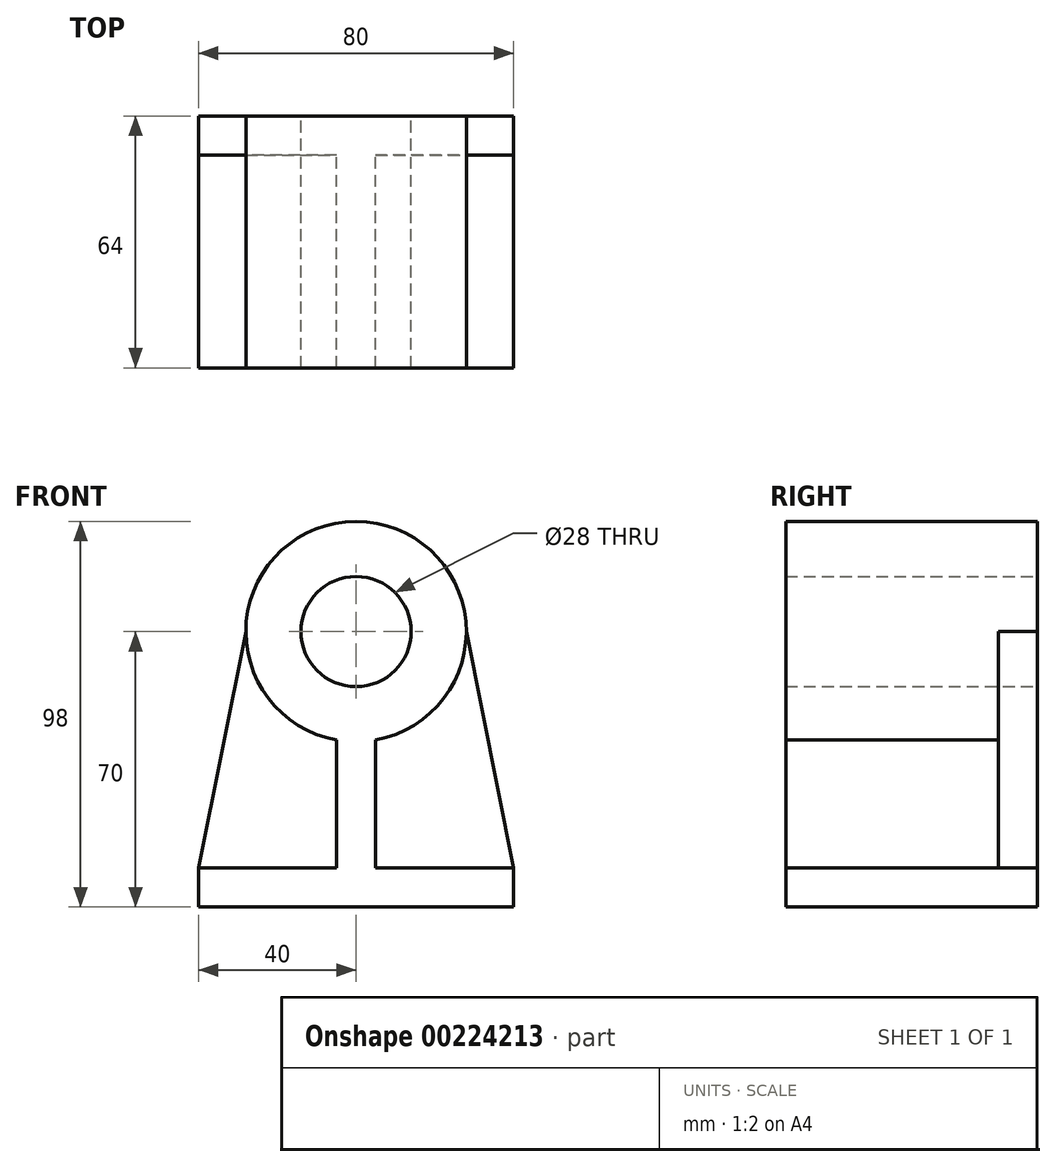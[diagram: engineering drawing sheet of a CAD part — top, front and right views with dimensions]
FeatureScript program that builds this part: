
annotation { "Feature Type Name" : "Feature", "Feature Type Description" : "" }
export const myFeature = defineFeature(function(context is Context, id is Id, definition is map)
    precondition{}
    {
        {
            var Q0;
            Q0=qCreatedBy(makeId("Front.planeOp"),FACE);
            var sketch = newSketch(context, id + "F0", { "sketchPlane" : qUnion([Q0])});
            skLineSegment(sketch, "E0", {"start": v(0, 0) * mm, "end": v(80, 0) * mm});
            skLineSegment(sketch, "E1", {"start": v(80, 0) * mm, "end": v(80, 10) * mm});
            skLineSegment(sketch, "E2", {"start": v(80, 10) * mm, "end": v(45, 10) * mm});
            skLineSegment(sketch, "E3", {"start": v(45, 10) * mm, "end": v(45, 42.45) * mm});
            skLineSegment(sketch, "E4", {"start": v(35, 42.45) * mm, "end": v(35, 10) * mm});
            skLineSegment(sketch, "E5", {"start": v(35, 10) * mm, "end": v(0, 10) * mm});
            skLineSegment(sketch, "E6", {"start": v(0, 10) * mm, "end": v(0, 0) * mm});
            skLineSegment(sketch, "E7", {"start": v(40, -26.89) * mm, "end": v(40, 136.2) * mm, "construction": true});
            skArc(sketch, "E8", {"start": v(45, 42.45) * mm, "mid": v(40, 98) * mm, "end": v(35, 42.45) * mm});
            skCircle(sketch, "E9", {"center": v(40, 70) * mm, "radius": 14 * mm});
            skLineSegment(sketch, "E10", {"start": v(-15.81, 70) * mm, "end": v(116.4, 70) * mm, "construction": true});
            skLineSegment(sketch, "E11", {"start": v(0, 10) * mm, "end": v(8, 49.97) * mm});
            skLineSegment(sketch, "E12", {"start": v(80, 10) * mm, "end": v(68, 70) * mm});
            skLineSegment(sketch, "E13", {"start": v(8, 49.97) * mm, "end": v(12, 70) * mm});
            skSolve(sketch);
        }
        {
            var Q0;
            Q0=makeQuery(id+"F0.imprint","IMPRINT",FACE,{"disambiguationData":[TD([[makeQuery(id+"F0.imprint","IMPRINT",EDGE,{"derivedFrom":sQuery(id+"F0.wireOp",EDGE,"E0")}),1.0]])]});
            extrude(context, id + "F1", {"entities" : qUnion([Q0]), "depth" : 64 * mm});
        }
        {
            var Q0;
            {var subQ0=sQuery(id+"F0.wireOp",EDGE,"E4");Q0=makeQuery(id+"F0.imprint","IMPRINT",FACE,{"disambiguationData":[TD([[makeQuery(id+"F0.imprint","IMPRINT",EDGE,{"derivedFrom":subQ0}),-1.0]])]});}
            var Q1;
            Q1=makeQuery(id+"F0.imprint","IMPRINT",FACE,{"disambiguationData":[TD([[makeQuery(id+"F0.imprint","IMPRINT",EDGE,{"derivedFrom":sQuery(id+"F0.wireOp",EDGE,"E2")}),-1.0]])]});
            extrude(context, id + "F2", {"entities" : qUnion([Q0, Q1]), "operationType" : NewBodyOperationType.ADD, "depth" : 10 * mm});
        }
    });
